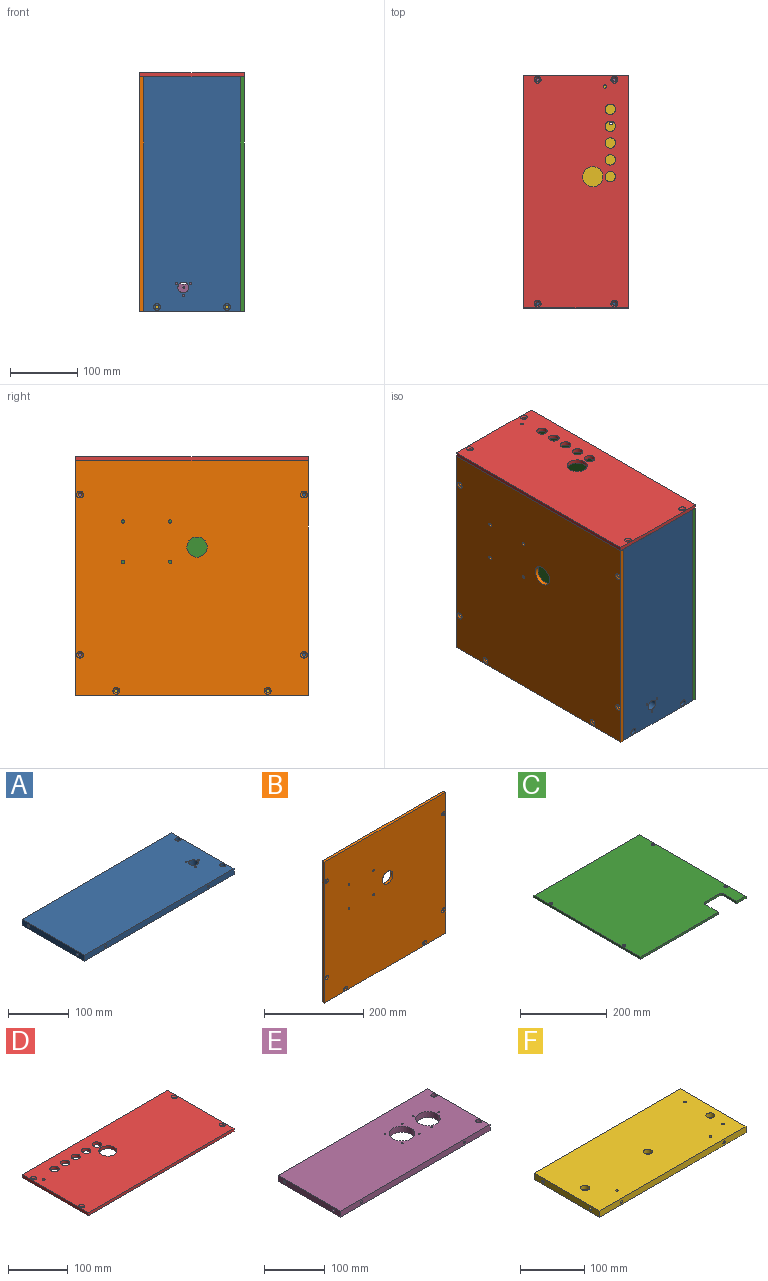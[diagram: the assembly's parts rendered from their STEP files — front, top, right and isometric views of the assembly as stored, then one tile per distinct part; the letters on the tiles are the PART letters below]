
ASSEMBLY  parts=6 mates=5
PART A: 28 faces, bbox 348x144x12 mm
  f0: plane 144x12mm, normal (1,0,0), area 1728mm2, adj f1,f3,f4,f5
  f1: plane 348x12mm, normal (0,1,0), area 4136.7mm2, adj f0,f2,f4,f5,f16,f18
  f2: plane 144x12mm, normal (-1,0,0), area 1688.7mm2, adj f1,f3,f4,f5,f24,f26
  f3: plane 348x12mm, normal (0,-1,0), area 4136.7mm2, adj f0,f2,f4,f5,f20,f22
  f4: plane 348x144mm, normal (0,0,1), area 49732.7mm2, adj f0,f1,f2,f3,f8,f11,f12,f13
  f5: plane 348x144mm, normal (0,0,-1), area 49842.2mm2, adj f0,f1,f2,f3,f6,f9,f12,f13
  f6: cylinder r=2.75mm len=6.6mm, axis (0,0,1), area 114mm2, adj f5,f7
  f7: plane 10x10mm, normal (0,0,1), area 54.8mm2, adj f6,f8
  f8: cylinder r=5mm len=10mm, axis (0,0,1), area 169.6mm2, adj f4,f7
  f9: cylinder r=2.75mm len=6.6mm, axis (0,0,1), area 114mm2, adj f5,f10
  f10: plane 10x10mm, normal (0,0,1), area 54.8mm2, adj f9,f11
  f11: cylinder r=5mm len=10mm, axis (0,0,1), area 169.6mm2, adj f4,f10
  f12: cylinder r=1.5mm len=12mm, axis (0,0,1), area 113.1mm2, adj f4,f5
  f13: cylinder r=1.5mm len=12mm, axis (0,0,1), area 113.1mm2, adj f4,f5
  f14: cylinder r=8mm len=16mm, axis (0,0,1), area 603.2mm2, adj f4,f5
  f15: cylinder r=1.5mm len=12mm, axis (0,0,1), area 113.1mm2, adj f4,f5
  f16: cylinder r=2.5mm len=15mm, axis (0,1,0), area 235.6mm2, adj f1,f17
  f17: plane 5x5mm, normal (0,1,0), area 19.6mm2, adj f16
  f18: cylinder r=2.5mm len=15mm, axis (0,1,0), area 235.6mm2, adj f1,f19
  f19: plane 5x5mm, normal (0,1,0), area 19.6mm2, adj f18
  f20: cylinder r=2.5mm len=15mm, axis (0,-1,0), area 235.6mm2, adj f3,f21
  f21: plane 5x5mm, normal (0,-1,0), area 19.6mm2, adj f20
  f22: cylinder r=2.5mm len=15mm, axis (0,-1,0), area 235.6mm2, adj f3,f23
  f23: plane 5x5mm, normal (0,-1,0), area 19.6mm2, adj f22
  f24: cylinder r=2.5mm len=15mm, axis (-1,0,0), area 235.6mm2, adj f2,f25
  f25: plane 5x5mm, normal (-1,0,0), area 19.6mm2, adj f24
  f26: cylinder r=2.5mm len=15mm, axis (-1,0,0), area 235.6mm2, adj f2,f27
  f27: plane 5x5mm, normal (-1,0,0), area 19.6mm2, adj f26
PART B: 23 faces, bbox 345x6x348 mm
  f0: plane 348x6mm, normal (1,0,0), area 2088mm2, adj f1,f3,f4,f5
  f1: plane 345x6mm, normal (0,0,1), area 2070mm2, adj f0,f2,f4,f5
  f2: plane 348x6mm, normal (-1,0,0), area 2088mm2, adj f1,f3,f4,f5
  f3: plane 345x6mm, normal (0,0,-1), area 2070mm2, adj f0,f2,f4,f5
  f4: plane 348x345mm, normal (0,-1,0), area 118803.4mm2, adj f0,f1,f2,f3,f6,f7,f8,f9
  f5: plane 348x345mm, normal (0,1,0), area 119132.1mm2, adj f0,f1,f2,f3,f6,f7,f8,f9
  f6: cylinder r=15mm len=30mm, axis (0,-1,0), area 565.5mm2, adj f4,f5
  f7: cylinder r=2.5mm len=6mm, axis (0,-1,0), area 94.2mm2, adj f4,f5
  f8: cylinder r=2.5mm len=6mm, axis (0,-1,0), area 94.2mm2, adj f4,f5
  f9: cylinder r=2.5mm len=6mm, axis (0,-1,0), area 94.2mm2, adj f4,f5
  f10: cylinder r=2.5mm len=6mm, axis (0,-1,0), area 94.2mm2, adj f4,f5
  f11: cylinder r=2.75mm len=5.5mm, axis (0,-1,0), area 64.8mm2, adj f5,f12
  f12: cone r=2.75mm half-angle=45deg, axis (0,-1,0), area 77.5mm2, adj f4,f11
  f13: cylinder r=2.75mm len=5.5mm, axis (0,-1,0), area 64.8mm2, adj f5,f14
  f14: cone r=2.75mm half-angle=45deg, axis (0,-1,0), area 77.5mm2, adj f4,f13
  f15: cylinder r=2.75mm len=5.5mm, axis (0,-1,0), area 64.8mm2, adj f5,f16
  f16: cone r=2.75mm half-angle=45deg, axis (0,-1,0), area 77.5mm2, adj f4,f15
  f17: cylinder r=2.75mm len=5.5mm, axis (0,-1,0), area 64.8mm2, adj f5,f18
  f18: cone r=2.75mm half-angle=45deg, axis (0,-1,0), area 77.5mm2, adj f4,f17
  f19: cylinder r=2.75mm len=5.5mm, axis (0,-1,0), area 64.8mm2, adj f5,f20
  f20: cone r=2.75mm half-angle=45deg, axis (0,-1,0), area 77.5mm2, adj f4,f19
  f21: cylinder r=2.75mm len=5.5mm, axis (0,-1,0), area 64.8mm2, adj f5,f22
  f22: cone r=2.75mm half-angle=45deg, axis (0,-1,0), area 77.5mm2, adj f4,f21
PART C: 20 faces, bbox 345x348x6 mm
  f0: plane 45x6mm, normal (-1,0,0), area 270mm2, adj f1,f9,f10,f11
  f1: plane 30x6mm, normal (0,-1,0), area 180mm2, adj f0,f2,f10,f11
  f2: plane 348x6mm, normal (1,0,0), area 2088mm2, adj f1,f3,f10,f11
  f3: plane 345x6mm, normal (0,1,0), area 2070mm2, adj f2,f4,f10,f11
  f4: plane 348x6mm, normal (-1,0,0), area 2088mm2, adj f3,f5,f10,f11
  f5: plane 255x6mm, normal (0,-1,0), area 1530mm2, adj f4,f6,f10,f11
  f6: plane 45x6mm, normal (1,0,0), area 270mm2, adj f5,f7,f10,f11
  f7: cylinder r=5mm len=6mm, axis (0,0,-1), area 47.1mm2, adj f6,f8,f10,f11
  f8: plane 50x6mm, normal (0,-1,0), area 300mm2, adj f7,f9,f10,f11
  f9: cylinder r=5mm len=6mm, axis (0,0,-1), area 47.1mm2, adj f0,f8,f10,f11
  f10: plane 348x345mm, normal (0,0,1), area 116843.8mm2, adj f0,f1,f2,f3,f4,f5,f6,f7
  f11: plane 348x345mm, normal (0,0,-1), area 116975.7mm2, adj f0,f1,f2,f3,f4,f5,f6,f7
  f12: cylinder r=2.75mm len=5.5mm, axis (0,0,1), area 77.8mm2, adj f11,f13
  f13: cone r=2.75mm half-angle=45deg, axis (0,0,1), area 46.7mm2, adj f10,f12
  f14: cylinder r=2.75mm len=5.5mm, axis (0,0,1), area 77.8mm2, adj f11,f15
  f15: cone r=2.75mm half-angle=45deg, axis (0,0,1), area 46.7mm2, adj f10,f14
  f16: cylinder r=2.75mm len=5.5mm, axis (0,0,1), area 77.8mm2, adj f11,f17
  f17: cone r=2.75mm half-angle=45deg, axis (0,0,1), area 46.7mm2, adj f10,f16
  f18: cylinder r=2.75mm len=5.5mm, axis (0,0,1), area 77.8mm2, adj f11,f19
  f19: cone r=2.75mm half-angle=45deg, axis (0,0,1), area 46.7mm2, adj f10,f18
PART D: 21 faces, bbox 345x156x6 mm
  f0: plane 156x6mm, normal (1,0,0), area 936mm2, adj f1,f9,f11,f12
  f1: plane 345x6mm, normal (0,1,0), area 2070mm2, adj f0,f2,f11,f12
  f2: plane 156x6mm, normal (-1,0,0), area 936mm2, adj f1,f9,f11,f12
  f3: cylinder r=7.75mm len=15.5mm, axis (0,0,-1), area 292.2mm2, adj f11,f12
  f4: cylinder r=7.75mm len=15.5mm, axis (0,0,-1), area 292.2mm2, adj f11,f12
  f5: cylinder r=7.75mm len=15.5mm, axis (0,0,-1), area 292.2mm2, adj f11,f12
  f6: cylinder r=7.75mm len=15.5mm, axis (0,0,-1), area 292.2mm2, adj f11,f12
  f7: cylinder r=7.75mm len=15.5mm, axis (0,0,-1), area 292.2mm2, adj f11,f12
  f8: cylinder r=15mm len=30mm, axis (0,0,-1), area 565.5mm2, adj f11,f12
  f9: plane 345x6mm, normal (0,-1,0), area 2070mm2, adj f0,f2,f11,f12
  f10: cylinder r=2.5mm len=6mm, axis (0,0,-1), area 94.2mm2, adj f11,f12
  f11: plane 345x156mm, normal (0,0,1), area 51835.9mm2, adj f0,f1,f2,f3,f4,f5,f6,f7
  f12: plane 345x156mm, normal (0,0,-1), area 52055mm2, adj f0,f1,f2,f3,f4,f5,f6,f7
  f13: cylinder r=2.75mm len=5.5mm, axis (0,0,1), area 64.8mm2, adj f12,f14
  f14: cone r=2.75mm half-angle=45deg, axis (0,0,1), area 77.5mm2, adj f11,f13
  f15: cylinder r=2.75mm len=5.5mm, axis (0,0,1), area 64.8mm2, adj f12,f16
  f16: cone r=2.75mm half-angle=45deg, axis (0,0,1), area 77.5mm2, adj f11,f15
  f17: cylinder r=2.75mm len=5.5mm, axis (0,0,1), area 64.8mm2, adj f12,f18
  f18: cone r=2.75mm half-angle=45deg, axis (0,0,1), area 77.5mm2, adj f11,f17
  f19: cylinder r=2.75mm len=5.5mm, axis (0,0,1), area 64.8mm2, adj f12,f20
  f20: cone r=2.75mm half-angle=45deg, axis (0,0,1), area 77.5mm2, adj f11,f19
PART E: 33 faces, bbox 348x144x12 mm
  f0: plane 144x12mm, normal (1,0,0), area 1728mm2, adj f1,f3,f4,f5
  f1: plane 348x12mm, normal (0,1,0), area 4136.7mm2, adj f0,f2,f4,f5,f16,f18
  f2: plane 144x12mm, normal (-1,0,0), area 1688.7mm2, adj f1,f3,f4,f5,f24,f26
  f3: plane 348x12mm, normal (0,-1,0), area 4136.7mm2, adj f0,f2,f4,f5,f20,f22
  f4: plane 348x144mm, normal (0,0,1), area 47263.4mm2, adj f0,f1,f2,f3,f8,f11,f12,f13
  f5: plane 348x144mm, normal (0,0,-1), area 47372.9mm2, adj f0,f1,f2,f3,f6,f9,f12,f13
  f6: cylinder r=2.75mm len=6.6mm, axis (0,0,1), area 114mm2, adj f5,f7
  f7: plane 10x10mm, normal (0,0,1), area 54.8mm2, adj f6,f8
  f8: cylinder r=5mm len=10mm, axis (0,0,1), area 169.6mm2, adj f4,f7
  f9: cylinder r=2.75mm len=6.6mm, axis (0,0,1), area 114mm2, adj f5,f10
  f10: plane 10x10mm, normal (0,0,1), area 54.8mm2, adj f9,f11
  f11: cylinder r=5mm len=10mm, axis (0,0,1), area 169.6mm2, adj f4,f10
  f12: cylinder r=1.5mm len=12mm, axis (0,0,1), area 113.1mm2, adj f4,f5
  f13: cylinder r=1.5mm len=12mm, axis (0,0,1), area 113.1mm2, adj f4,f5
  f14: cylinder r=20mm len=40mm, axis (0,0,1), area 1508mm2, adj f4,f5
  f15: cylinder r=1.5mm len=12mm, axis (0,0,1), area 113.1mm2, adj f4,f5
  f16: cylinder r=2.5mm len=15mm, axis (0,1,0), area 235.6mm2, adj f1,f17
  f17: plane 5x5mm, normal (0,1,0), area 19.6mm2, adj f16
  f18: cylinder r=2.5mm len=15mm, axis (0,1,0), area 235.6mm2, adj f1,f19
  f19: plane 5x5mm, normal (0,1,0), area 19.6mm2, adj f18
  f20: cylinder r=2.5mm len=15mm, axis (0,-1,0), area 235.6mm2, adj f3,f21
  f21: plane 5x5mm, normal (0,-1,0), area 19.6mm2, adj f20
  f22: cylinder r=2.5mm len=15mm, axis (0,-1,0), area 235.6mm2, adj f3,f23
  f23: plane 5x5mm, normal (0,-1,0), area 19.6mm2, adj f22
  f24: cylinder r=2.5mm len=15mm, axis (-1,0,0), area 235.6mm2, adj f2,f25
  f25: plane 5x5mm, normal (-1,0,0), area 19.6mm2, adj f24
  f26: cylinder r=2.5mm len=15mm, axis (-1,0,0), area 235.6mm2, adj f2,f27
  f27: plane 5x5mm, normal (-1,0,0), area 19.6mm2, adj f26
  f28: cylinder r=21mm len=42mm, axis (0,0,1), area 1583.4mm2, adj f4,f5
  f29: cylinder r=1.5mm len=12mm, axis (0,0,1), area 113.1mm2, adj f4,f5
  f30: cylinder r=1.5mm len=12mm, axis (0,0,1), area 113.1mm2, adj f4,f5
  f31: cylinder r=1.5mm len=12mm, axis (0,0,1), area 113.1mm2, adj f4,f5
  f32: cylinder r=1.5mm len=12mm, axis (0,0,1), area 113.1mm2, adj f4,f5
PART F: 35 faces, bbox 321x144x12 mm
  f0: plane 144x12mm, normal (1,0,0), area 1688.7mm2, adj f1,f3,f4,f5,f27,f29
  f1: plane 321x12mm, normal (0,1,0), area 3812.7mm2, adj f0,f2,f4,f5,f19,f21
  f2: plane 144x12mm, normal (-1,0,0), area 1688.7mm2, adj f1,f3,f4,f5,f23,f25
  f3: plane 321x12mm, normal (0,-1,0), area 3812.7mm2, adj f0,f2,f4,f5,f31,f33
  f4: plane 321x144mm, normal (0,0,1), area 45711.9mm2, adj f0,f1,f2,f3,f8,f11,f14,f15
  f5: plane 321x144mm, normal (0,0,-1), area 46003.5mm2, adj f0,f1,f2,f3,f6,f9,f12,f15
  f6: cylinder r=4.25mm len=8.5mm, axis (0,0,1), area 93.5mm2, adj f5,f7
  f7: plane 14x14mm, normal (0,0,1), area 97.2mm2, adj f6,f8
  f8: cylinder r=7mm len=14mm, axis (0,0,1), area 373.8mm2, adj f4,f7
  f9: cylinder r=4.25mm len=8.5mm, axis (0,0,1), area 93.5mm2, adj f5,f10
  f10: plane 14x14mm, normal (0,0,1), area 97.2mm2, adj f9,f11
  f11: cylinder r=7mm len=14mm, axis (0,0,1), area 373.8mm2, adj f4,f10
  f12: cylinder r=4.25mm len=8.5mm, axis (0,0,1), area 93.5mm2, adj f5,f13
  f13: plane 14x14mm, normal (0,0,1), area 97.2mm2, adj f12,f14
  f14: cylinder r=7mm len=14mm, axis (0,0,1), area 373.8mm2, adj f4,f13
  f15: cylinder r=2mm len=12mm, axis (0,0,1), area 150.8mm2, adj f4,f5
  f16: cylinder r=2mm len=12mm, axis (0,0,1), area 150.8mm2, adj f4,f5
  f17: cylinder r=2mm len=12mm, axis (0,0,1), area 150.8mm2, adj f4,f5
  f18: cylinder r=2mm len=12mm, axis (0,0,1), area 150.8mm2, adj f4,f5
  f19: cylinder r=2.5mm len=15mm, axis (0,1,0), area 235.6mm2, adj f1,f20
  f20: plane 5x5mm, normal (0,1,0), area 19.6mm2, adj f19
  f21: cylinder r=2.5mm len=15mm, axis (0,1,0), area 235.6mm2, adj f1,f22
  f22: plane 5x5mm, normal (0,1,0), area 19.6mm2, adj f21
  f23: cylinder r=2.5mm len=15mm, axis (-1,0,0), area 235.6mm2, adj f2,f24
  f24: plane 5x5mm, normal (-1,0,0), area 19.6mm2, adj f23
  f25: cylinder r=2.5mm len=15mm, axis (-1,0,0), area 235.6mm2, adj f2,f26
  f26: plane 5x5mm, normal (-1,0,0), area 19.6mm2, adj f25
  f27: cylinder r=2.5mm len=15mm, axis (1,0,0), area 235.6mm2, adj f0,f28
  f28: plane 5x5mm, normal (1,0,0), area 19.6mm2, adj f27
  f29: cylinder r=2.5mm len=15mm, axis (1,0,0), area 235.6mm2, adj f0,f30
  f30: plane 5x5mm, normal (1,0,0), area 19.6mm2, adj f29
  f31: cylinder r=2.5mm len=15mm, axis (0,-1,0), area 235.6mm2, adj f3,f32
  f32: plane 5x5mm, normal (0,-1,0), area 19.6mm2, adj f31
  f33: cylinder r=2.5mm len=15mm, axis (0,-1,0), area 235.6mm2, adj f3,f34
  f34: plane 5x5mm, normal (0,-1,0), area 19.6mm2, adj f33
PLACE A rot(axis=(0.58,0.58,-0.58),120deg) t=(213.59,-418.9,-128.94)mm
PLACE B rot(axis=(0,0,-1),90deg) t=(141.59,-258.4,-128.94)mm
PLACE C rot(axis=(0.58,0.58,0.58),120deg) t=(285.59,-258.4,-128.94)mm
PLACE D rot(axis=(0,0,-1),90deg) t=(213.59,-258.4,45.06)mm
PLACE E rot(axis=(-0.58,0.58,0.58),120deg) t=(213.59,-97.9,-128.94)mm
PLACE F rot(axis=(0,0,1),90deg) t=(213.59,-258.4,-302.94)mm
MATE fastened E.f9 <-> F.f23  axis (0,-1,0) through (265.59,-97.9,-296.94)mm
MATE fastened A.f6 <-> F.f23  axis (0,1,0) through (265.59,-418.9,-296.94)mm
MATE fastened F.f21 <-> B.f13  axis (-1,0,0) through (141.59,-370.9,-296.94)mm
MATE fastened C.f16 <-> E.f16  axis (-1,0,0) through (285.59,-91.9,-4.94)mm
MATE fastened D.f15 <-> A.f26  axis (0,0,-1) through (156.59,-424.9,45.06)mm
